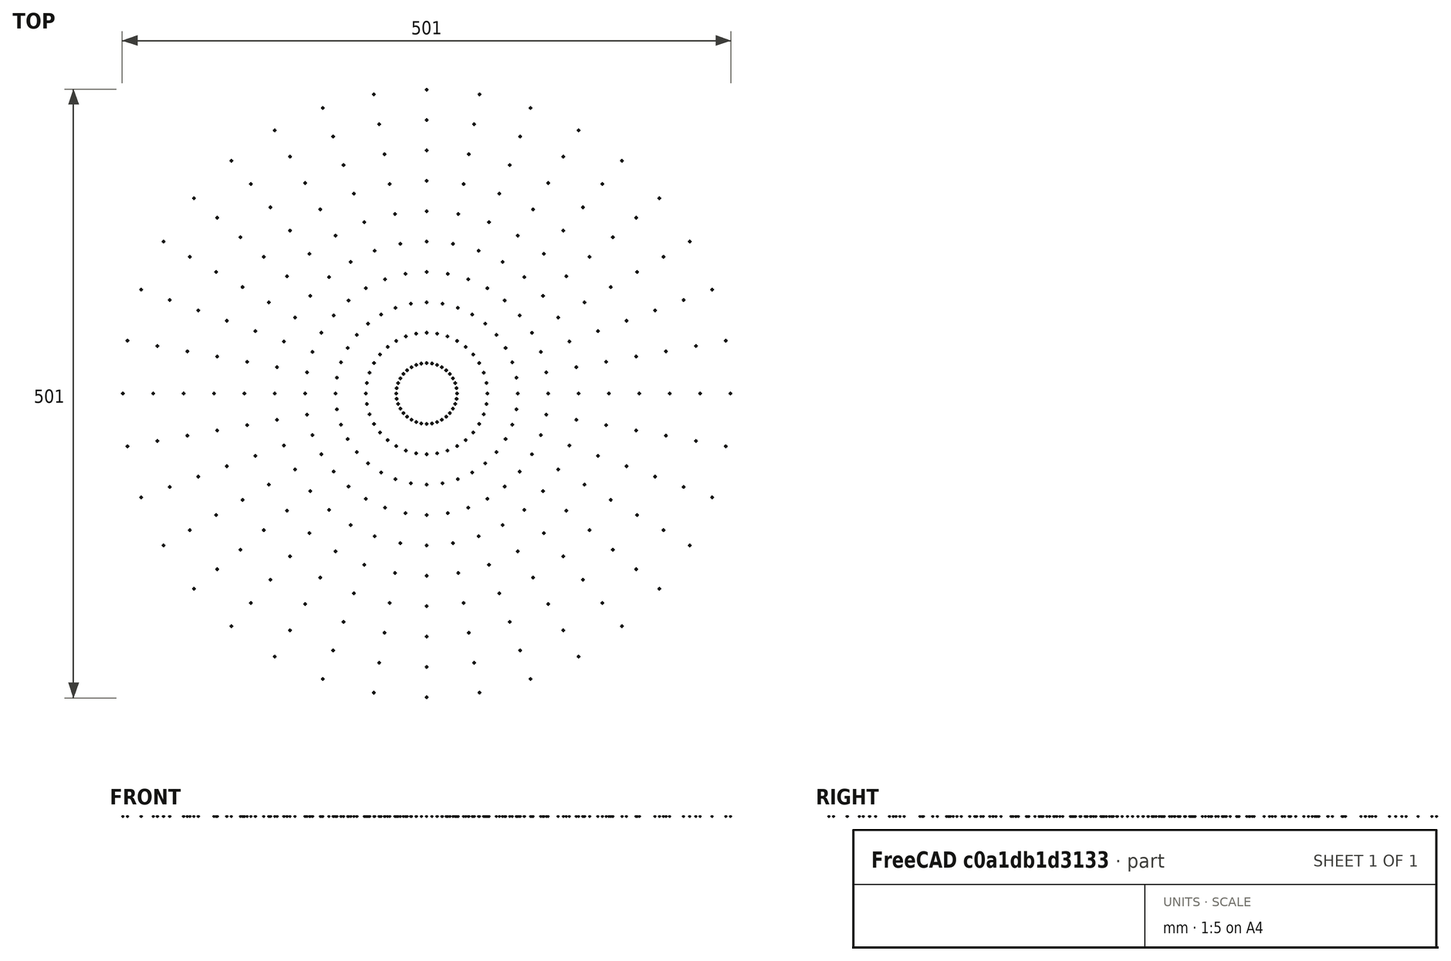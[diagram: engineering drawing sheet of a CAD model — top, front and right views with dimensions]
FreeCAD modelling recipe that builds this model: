
FCSTD DOCUMENT  (FreeCAD 0.16RUnknown)
Label: model-board
License: All rights reserved
LicenseURL: http://en.wikipedia.org/wiki/All_rights_reserved
objects: Part::Part2DObjectPython×4, Part::FeaturePython×2, Spreadsheet::Sheet×1
note: 6 computed .brp shape members not serialized (recipe doc carries the construction recipe); baked Part::Feature solids carry a one-line shape summary decoded from their .brp

FEATURE [Part::Part2DObjectPython] Circle  label="circleExternal"  # Draft 2D object (typed FeaturePython)
  FirstAngle = 0
  LastAngle = 360
  MakeFace = true
  Radius = 300
  expr: Radius = prefs.circleExternal / 2
FEATURE [Part::Part2DObjectPython] Rectangle  label="servo"  # Draft 2D object (typed FeaturePython)
  ChamferSize = 0
  Columns = 1
  FilletRadius = 0
  Height = 41
  Length = 20
  MakeFace = true
  Placement = pos=(-10,174,0) rot=(0,0,1;0rad)
  Rows = 1
  expr: Placement.Base.y = (prefs.circleExternal + prefs.circleInternal - 2 * prefs.servoLength) / 4
  expr: Height = prefs.servoLength
  expr: Placement.Base.x = -prefs.servoWidth / 2
FEATURE [Part::Part2DObjectPython] Circle002  label="screw"  # Draft 2D object (typed FeaturePython)
  FirstAngle = 0
  LastAngle = 0
  MakeFace = true
  Placement = pos=(0,25,0) rot=(0,0,1;0rad)
  Radius = 0.5
  expr: Radius = prefs.screwDiameter / 2
  expr: Placement.Base.x = 0
FEATURE [Part::FeaturePython] Array001  label="screwArray"  # Draft array (typed FeaturePython)
  Angle = 360
  ArrayType = 0
  Axis = (0,0,1)
  Base = -> Circle002
  Center = (0,0,0)
  Fuse = false
  IntervalAxis = (0,0,0)
  IntervalX = (1,0,0)
  IntervalY = (0,25,0)
  IntervalZ = (0,0,0)
  NumberPolar = 3
  NumberX = 1
  NumberY = 10
  NumberZ = 1
  expr: NumberPolar = prefs.servoNumber
FEATURE [Spreadsheet::Sheet] Spreadsheet  label="prefs"
  cells = A2=External circle diameter; B2(circleExternal)=600; C2=mm; A3=Internal circle diameter; B3(circleInternal)=178; C3=mm; A4=Number servo; B4(servoNumber)=3; C4=mm; A5=Diameter screw; B5(screwDiameter)=1; C5=mm; A6=Width servo; B6(servoWidth)=20; C6=mm; A7=Length servo; B7(servoLength)=41; C7=mm
FEATURE [Part::FeaturePython] Array  # Draft array (typed FeaturePython)
  Angle = 360
  ArrayType = 1
  Axis = (0,0,1)
  Base = -> Array001
  Center = (0,0,0)
  Fuse = false
  IntervalAxis = (0,0,0)
  IntervalX = (1,0,0)
  IntervalY = (0,1,0)
  IntervalZ = (0,0,0)
  NumberPolar = 36
  NumberX = 2
  NumberY = 2
  NumberZ = 1
FEATURE [Part::Part2DObjectPython] Circle003  label="screw001"  # Draft 2D object (typed FeaturePython)
  FirstAngle = 0
  LastAngle = 0
  MakeFace = true
  Placement = pos=(0,300,0) rot=(0,0,1;0rad)
  Radius = 0.5
  expr: Radius = prefs.screwDiameter / 2
  expr: Placement.Base.x = 0
